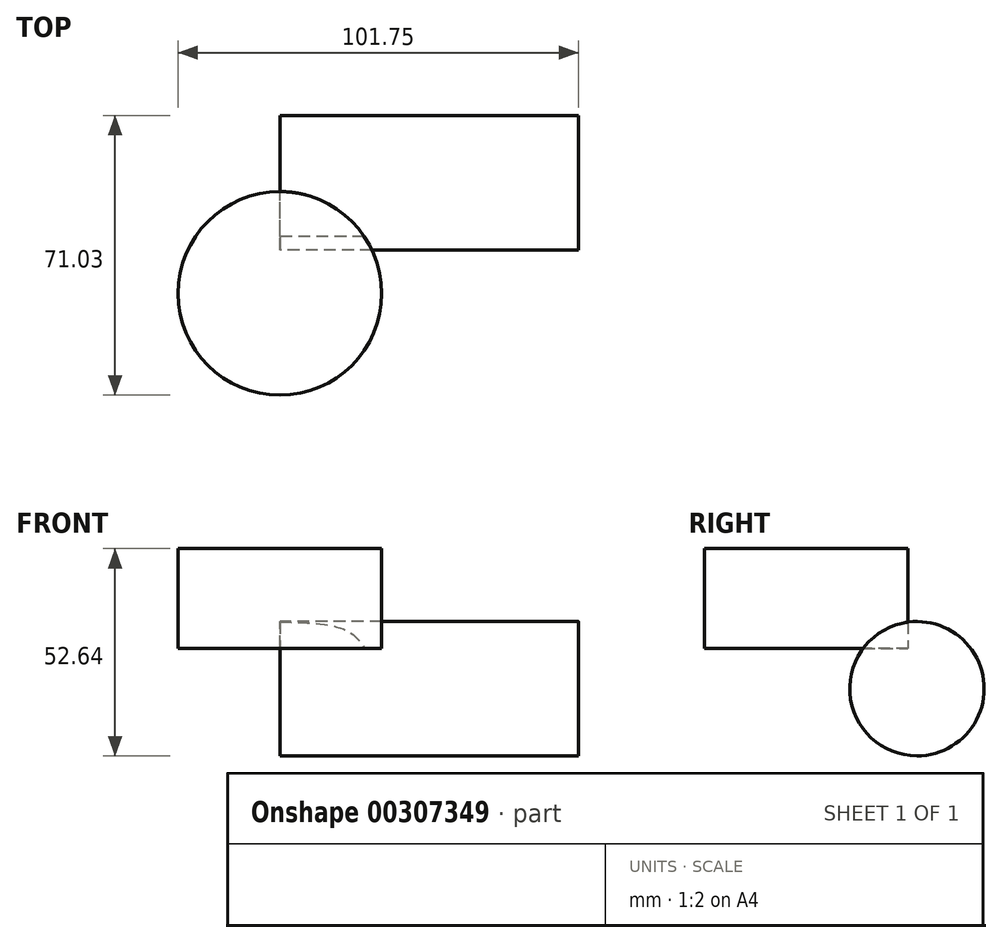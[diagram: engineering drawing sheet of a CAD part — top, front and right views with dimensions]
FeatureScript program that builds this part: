
annotation { "Feature Type Name" : "Feature", "Feature Type Description" : "" }
export const myFeature = defineFeature(function(context is Context, id is Id, definition is map)
    precondition{}
    {
        {
            var Q0;
            Q0=qCreatedBy(makeId("Top.planeOp"),FACE);
            var sketch = newSketch(context, id + "F0", { "sketchPlane" : qUnion([Q0])});
            skCircle(sketch, "E0", {"center": v(0, 0) * mm, "radius": 25.86 * mm});
            skSolve(sketch);
        }
        {
            var Q0;
            Q0 = qSketchRegion(id + "F0", true);
            extrude(context, id + "F1", {"entities" : qUnion([Q0]), "depth" : 25.4 * mm});
        }
        {
            var Q0;
            Q0=qCreatedBy(makeId("Right.planeOp"),FACE);
            var sketch = newSketch(context, id + "F2", { "sketchPlane" : qUnion([Q0])});
            skCircle(sketch, "E1", {"center": v(28.1, -10.17) * mm, "radius": 17.07 * mm});
            skSolve(sketch);
        }
        {
            var Q0;
            Q0 = qSketchRegion(id + "F2", true);
            extrude(context, id + "F3", {"entities" : qUnion([Q0]), "operationType" : NewBodyOperationType.ADD, "depth" : 75.9 * mm});
        }
    });
